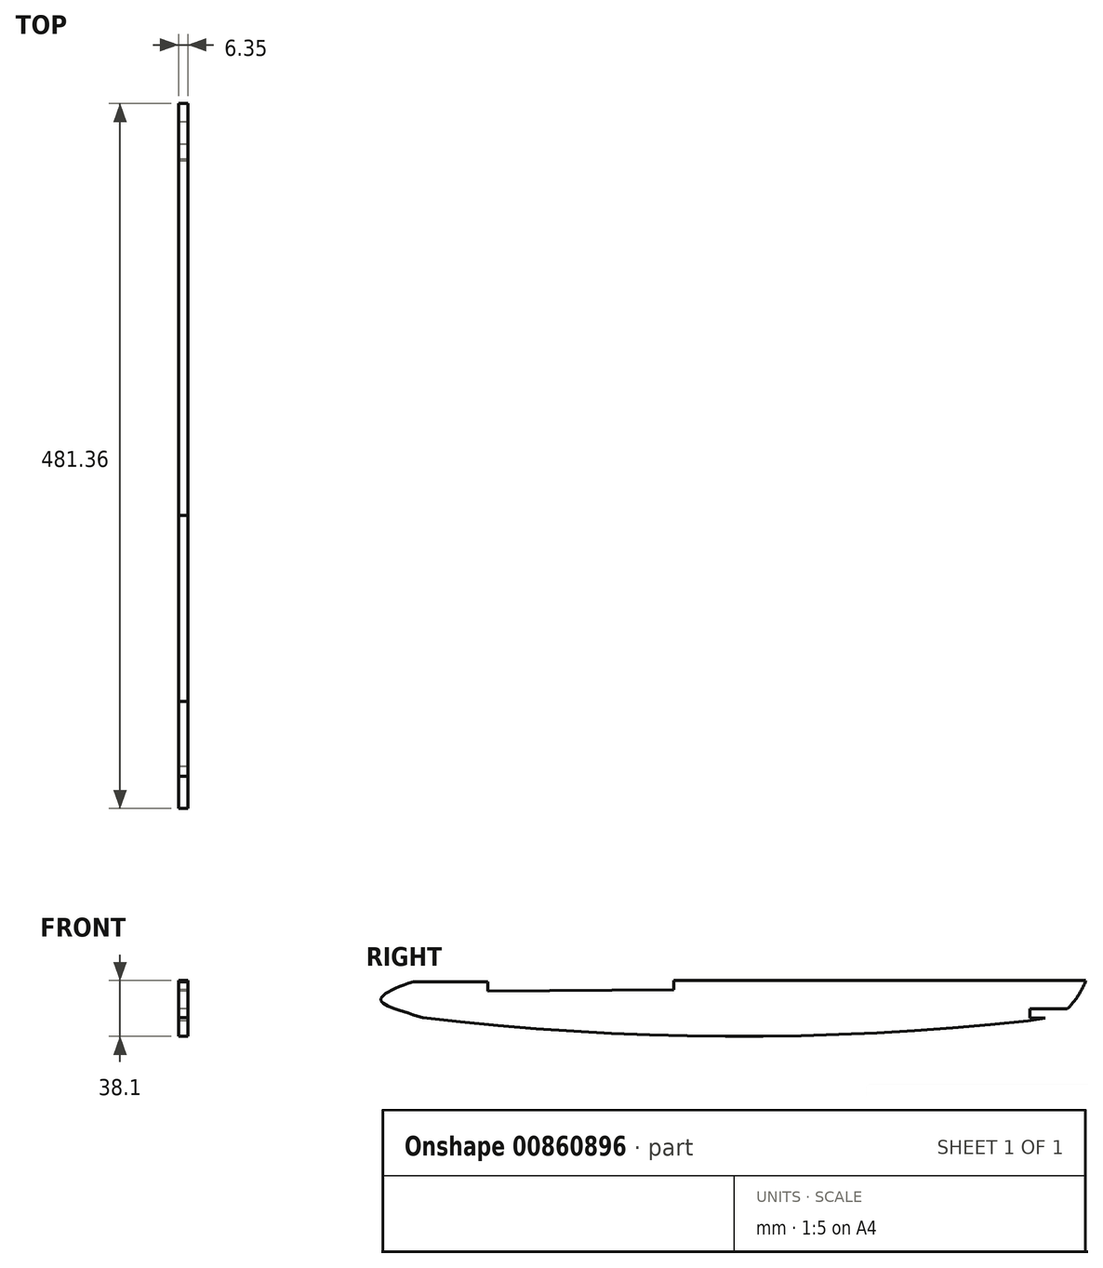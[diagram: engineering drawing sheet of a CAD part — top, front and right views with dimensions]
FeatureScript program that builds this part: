
annotation { "Feature Type Name" : "Feature", "Feature Type Description" : "" }
export const myFeature = defineFeature(function(context is Context, id is Id, definition is map)
    precondition{}
    {
        {
            var Q0;
            Q0=qCreatedBy(makeId("Right.planeOp"),FACE);
            var sketch = newSketch(context, id + "F0", { "sketchPlane" : qUnion([Q0])});
            skPoint(sketch, "E0.middle", {"position": v(0, 0) * mm});
            skLineSegment(sketch, "E1.trimOffspring", {"start": v(-151.9, 12.46) * mm, "end": v(-202.9, 12.7) * mm});
            skFitSpline(sketch, "E2", {"points": [v(-202.9, 12.7) * mm, v(-224.94, 0) * mm, v(-196.43, -11.95) * mm], "startDerivative": vector(-77.12, -25.4) * mm, "endDerivative": vector(77.12, -25.4) * mm});
            skPoint(sketch, "E3.orphan", {"position": v(-228.1, 12.82) * mm});
            skPoint(sketch, "E4.orphan", {"position": v(-221.78, -12.82) * mm});
            skLineSegment(sketch, "E5", {"start": v(-151.9, 12.46) * mm, "end": v(-151.9, 6.08) * mm});
            skLineSegment(sketch, "E6", {"start": v(-24.9, 13.4) * mm, "end": v(-24.9, 7.05) * mm});
            skLineSegment(sketch, "E7", {"start": v(-151.9, 6.08) * mm, "end": v(-24.9, 7.05) * mm});
            skArc(sketch, "E8", {"start": v(-196.43, -11.95) * mm, "mid": v(10.2, -24.67) * mm, "end": v(216.96, -14.06) * mm});
            skLineSegment(sketch, "E9", {"start": v(-24.9, 13.4) * mm, "end": v(256.4, 13.4) * mm});
            skFitSpline(sketch, "E10", {"points": [v(228.1, -12.82) * mm, v(256.4, 13.4) * mm], "startDerivative": vector(31.58, -0.15) * mm, "endDerivative": vector(18.75, 48.19) * mm});
            skLineSegment(sketch, "E11", {"start": v(228.64, -12.18) * mm, "end": v(216.96, -14.06) * mm});
            skLineSegment(sketch, "E12", {"start": v(243.76, -5.83) * mm, "end": v(218.36, -5.83) * mm});
            skLineSegment(sketch, "E13", {"start": v(218.36, -5.83) * mm, "end": v(218.36, -12.18) * mm});
            skLineSegment(sketch, "E14", {"start": v(218.36, -12.18) * mm, "end": v(228.64, -12.18) * mm});
            skSolve(sketch);
        }
        {
            var Q0;
            Q0 = qSketchRegion(id + "F0", true);
            extrude(context, id + "F1", {"entities" : qUnion([Q0]), "depth" : 6.35 * mm, "offsetDistance" : 25.4 * mm});
        }
    });
